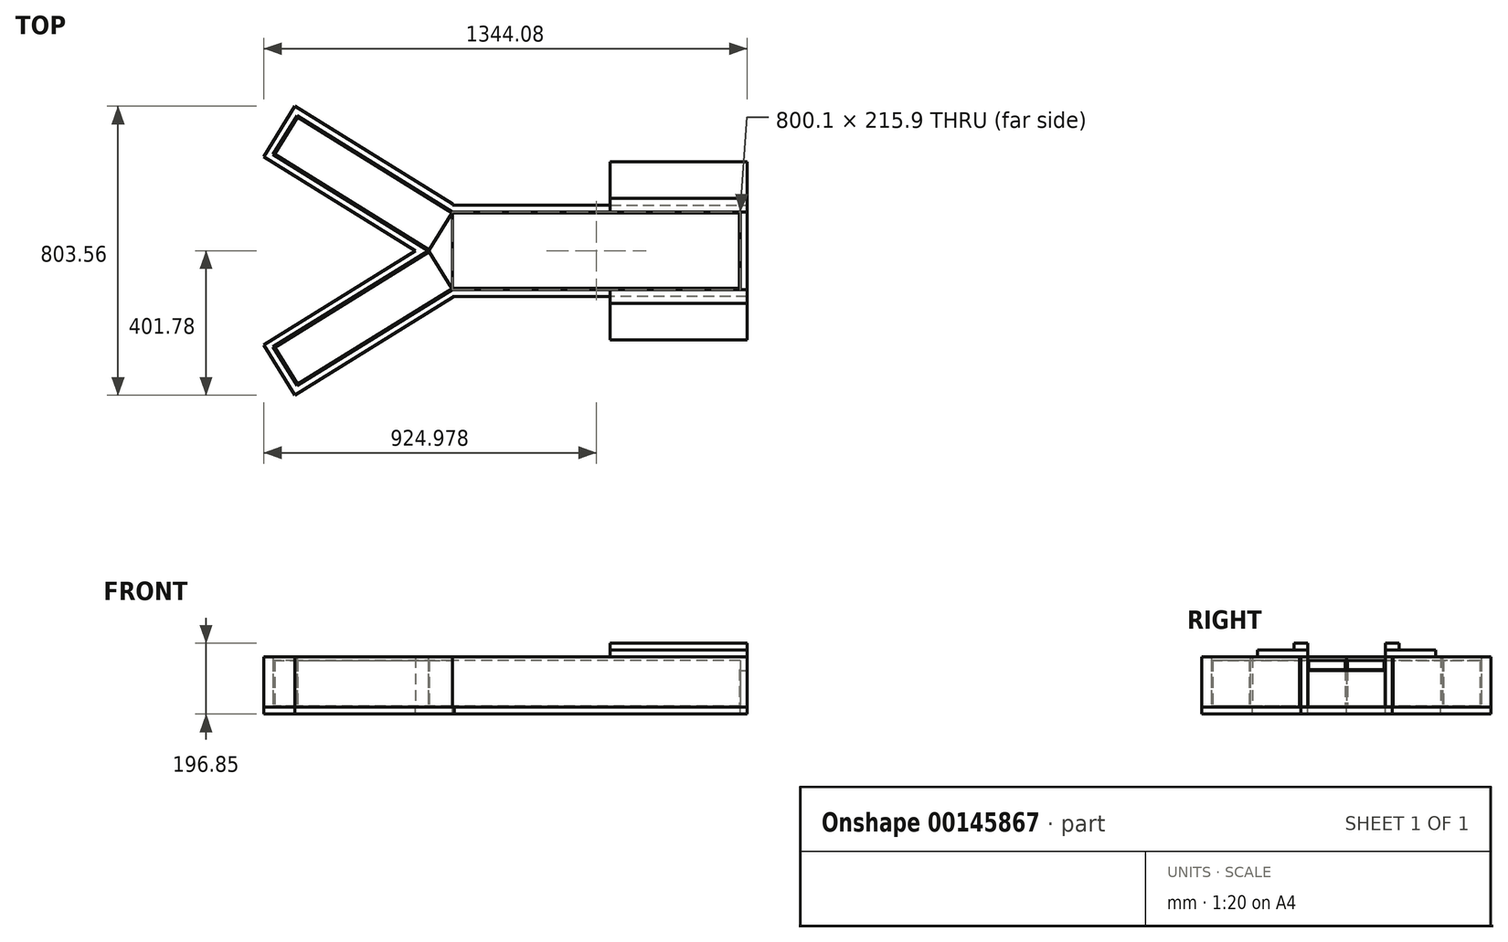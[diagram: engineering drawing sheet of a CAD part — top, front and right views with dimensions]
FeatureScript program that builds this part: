
annotation { "Feature Type Name" : "Feature", "Feature Type Description" : "" }
export const myFeature = defineFeature(function(context is Context, id is Id, definition is map)
    precondition{}
    {
        {
            var Q0;
            Q0=qCreatedBy(makeId("Top.planeOp"),FACE);
            var sketch = newSketch(context, id + "F0", { "sketchPlane" : qUnion([Q0])});
            skLineSegment(sketch, "E0", {"start": v(0, 0) * mm, "end": v(746.46, 0) * mm, "construction": true});
            skLineSegment(sketch, "E1", {"start": v(0, 0) * mm, "end": v(-518.9, 321.58) * mm, "construction": true});
            skLineSegment(sketch, "E2.0.MirrorCS", {"start": v(0, 0) * mm, "end": v(-518.9, -321.58) * mm, "construction": true});
            skLineSegment(sketch, "E3.bottom", {"start": v(746.46, -107.95) * mm, "end": v(-53.64, -107.95) * mm});
            skLineSegment(sketch, "E3.top", {"start": v(746.46, 107.95) * mm, "end": v(-53.64, 107.95) * mm});
            skLineSegment(sketch, "E3.left", {"start": v(746.46, 107.95) * mm, "end": v(746.46, -107.95) * mm});
            skLineSegment(sketch, "E3.right", {"start": v(-53.64, 107.95) * mm, "end": v(-53.64, -107.95) * mm});
            skLineSegment(sketch, "E4", {"start": v(-485.44, 375.56) * mm, "end": v(-552.34, 267.6) * mm});
            skLineSegment(sketch, "E5", {"start": v(-552.34, 267.6) * mm, "end": v(-120.54, 0) * mm});
            skLineSegment(sketch, "E6", {"start": v(-120.54, 0) * mm, "end": v(-53.64, 107.95) * mm});
            skLineSegment(sketch, "E7", {"start": v(-53.64, 107.95) * mm, "end": v(-485.44, 375.56) * mm});
            skLineSegment(sketch, "E8.0.MirrorCS", {"start": v(-53.64, -107.95) * mm, "end": v(-485.44, -375.56) * mm});
            skLineSegment(sketch, "E9.0.MirrorCS", {"start": v(-120.54, 0) * mm, "end": v(-53.64, -107.95) * mm});
            skLineSegment(sketch, "E10.0.MirrorCS", {"start": v(-552.34, -267.6) * mm, "end": v(-120.54, 0) * mm});
            skLineSegment(sketch, "E11.0.MirrorCS", {"start": v(-485.44, -375.56) * mm, "end": v(-552.34, -267.6) * mm});
            skSolve(sketch);
        }
        {
            var Q0;
            Q0=makeQuery(id+"F0.imprint","IMPRINT",FACE,{"disambiguationData":[TD([[makeQuery(id+"F0.imprint","IMPRINT",EDGE,{"derivedFrom":sQuery(id+"F0.wireOp",EDGE,"E4")}),1.0]])]});
            extrude(context, id + "F1", {"entities" : qUnion([Q0]), "depth" : 3.17 * mm});
        }
        {
            var Q0;
            Q0=makeQuery(id+"F0.imprint","IMPRINT",FACE,{"disambiguationData":[TD([[makeQuery(id+"F0.imprint","IMPRINT",EDGE,{"derivedFrom":sQuery(id+"F0.wireOp",EDGE,"E8.0.MirrorCS")}),-1.0]])]});
            extrude(context, id + "F2", {"entities" : qUnion([Q0]), "depth" : 3.17 * mm});
        }
        {
            var Q0;
            Q0=makeQuery(id+"F0.imprint","IMPRINT",FACE,{"disambiguationData":[TD([[makeQuery(id+"F0.imprint","IMPRINT",EDGE,{"derivedFrom":sQuery(id+"F0.wireOp",EDGE,"E3.right")}),-1.0]])]});
            extrude(context, id + "F3", {"entities" : qUnion([Q0]), "depth" : 3.17 * mm});
        }
        {
            var Q0;
            Q0=makeQuery(id+"F0.imprint","IMPRINT",FACE,{"disambiguationData":[TD([[makeQuery(id+"F0.imprint","IMPRINT",EDGE,{"derivedFrom":sQuery(id+"F0.wireOp",EDGE,"E3.bottom")}),-1.0]])]});
            extrude(context, id + "F4", {"entities" : qUnion([Q0]), "depth" : 3.17 * mm});
        }
        {
            var Q0;
            Q0=makeQuery(id+"F4.opExtrude","CAP_FACE",FACE,{"disambiguationData":[OSD([sQuery(id+"F0.wireOp",EDGE,"E3.bottom"),sQuery(id+"F0.wireOp",EDGE,"E3.top"),sQuery(id+"F0.wireOp",EDGE,"E3.left"),sQuery(id+"F0.wireOp",EDGE,"E3.right")])],"isStart":false});
            var sketch = newSketch(context, id + "F5", { "sketchPlane" : qUnion([Q0])});
            skLineSegment(sketch, "E12.0", {"start": v(-53.64, -104.78) * mm, "end": v(743.28, -104.78) * mm});
            skLineSegment(sketch, "E12.2", {"start": v(743.28, 104.78) * mm, "end": v(-53.64, 104.78) * mm});
            skLineSegment(sketch, "E12.3", {"start": v(743.28, -104.78) * mm, "end": v(743.28, 104.78) * mm});
            skLineSegment(sketch, "E13.0", {"start": v(-484.42, -371.18) * mm, "end": v(-55.31, -105.25) * mm});
            skLineSegment(sketch, "E13.1", {"start": v(-547.97, -268.63) * mm, "end": v(-484.42, -371.18) * mm});
            skLineSegment(sketch, "E13.2", {"start": v(-118.87, -2.7) * mm, "end": v(-547.97, -268.63) * mm});
            skLineSegment(sketch, "E14.0", {"start": v(-55.31, 105.25) * mm, "end": v(-484.42, 371.18) * mm});
            skLineSegment(sketch, "E14.2", {"start": v(-547.97, 268.63) * mm, "end": v(-118.87, 2.7) * mm});
            skLineSegment(sketch, "E14.3", {"start": v(-484.42, 371.18) * mm, "end": v(-547.97, 268.63) * mm});
            skLineSegment(sketch, "E15.0.0", {"start": v(-53.64, 107.95) * mm, "end": v(-485.44, 375.56) * mm});
            skLineSegment(sketch, "E15.0.1", {"start": v(-485.44, 375.56) * mm, "end": v(-552.34, 267.6) * mm});
            skLineSegment(sketch, "E15.0.2", {"start": v(-552.34, 267.6) * mm, "end": v(-120.54, 0) * mm});
            skLineSegment(sketch, "E16.0.0", {"start": v(-53.64, -107.95) * mm, "end": v(746.46, -107.95) * mm});
            skLineSegment(sketch, "E16.0.1", {"start": v(746.46, -107.95) * mm, "end": v(746.46, 107.95) * mm});
            skLineSegment(sketch, "E16.0.2", {"start": v(746.46, 107.95) * mm, "end": v(-53.64, 107.95) * mm});
            skLineSegment(sketch, "E17.0.0", {"start": v(-485.44, -375.56) * mm, "end": v(-53.64, -107.95) * mm});
            skLineSegment(sketch, "E17.0.2", {"start": v(-120.54, 0) * mm, "end": v(-552.34, -267.6) * mm});
            skLineSegment(sketch, "E17.0.3", {"start": v(-552.34, -267.6) * mm, "end": v(-485.44, -375.56) * mm});
            skLineSegment(sketch, "E18", {"start": v(-53.64, -104.78) * mm, "end": v(-53.64, -107.95) * mm});
            skLineSegment(sketch, "E19", {"start": v(-55.31, -105.25) * mm, "end": v(-53.64, -107.95) * mm});
            skLineSegment(sketch, "E20", {"start": v(-118.87, 2.7) * mm, "end": v(-120.54, 0) * mm});
            skLineSegment(sketch, "E21", {"start": v(-120.54, 0) * mm, "end": v(-118.87, -2.7) * mm});
            skLineSegment(sketch, "E22", {"start": v(-53.64, 104.78) * mm, "end": v(-53.64, 107.95) * mm});
            skLineSegment(sketch, "E23", {"start": v(-55.31, 105.25) * mm, "end": v(-53.64, 107.95) * mm});
            skLineSegment(sketch, "E24", {"start": v(-484.42, 371.18) * mm, "end": v(-487.11, 372.86) * mm});
            skLineSegment(sketch, "E25", {"start": v(-547.97, 268.63) * mm, "end": v(-550.67, 270.3) * mm});
            skLineSegment(sketch, "E26", {"start": v(-484.42, -371.18) * mm, "end": v(-487.11, -372.86) * mm});
            skLineSegment(sketch, "E27", {"start": v(-547.97, -268.63) * mm, "end": v(-550.67, -270.3) * mm});
            skLineSegment(sketch, "E28", {"start": v(743.28, -104.78) * mm, "end": v(746.46, -104.78) * mm});
            skLineSegment(sketch, "E29", {"start": v(743.28, 104.78) * mm, "end": v(746.46, 104.78) * mm});
            skSolve(sketch);
        }
        {
            var Q0;
            Q0=makeQuery(id+"F5.imprint","IMPRINT",FACE,{"disambiguationData":[TD([[makeQuery(id+"F5.imprint","IMPRINT",EDGE,{"derivedFrom":sQuery(id+"F5.wireOp",EDGE,"E13.0")}),-1.0]])]});
            extrude(context, id + "F6", {"entities" : qUnion([Q0]), "depth" : 127 * mm});
        }
        {
            var Q0;
            Q0=makeQuery(id+"F5.imprint","IMPRINT",FACE,{"disambiguationData":[TD([[makeQuery(id+"F5.imprint","IMPRINT",EDGE,{"derivedFrom":sQuery(id+"F5.wireOp",EDGE,"E13.1")}),-1.0]])]});
            extrude(context, id + "F7", {"entities" : qUnion([Q0]), "depth" : 127 * mm});
        }
        {
            var Q0;
            Q0=makeQuery(id+"F5.imprint","IMPRINT",FACE,{"disambiguationData":[TD([[makeQuery(id+"F5.imprint","IMPRINT",EDGE,{"derivedFrom":sQuery(id+"F5.wireOp",EDGE,"E13.2")}),-1.0]])]});
            extrude(context, id + "F8", {"entities" : qUnion([Q0]), "depth" : 127 * mm});
        }
        {
            var Q0;
            Q0=makeQuery(id+"F5.imprint","IMPRINT",FACE,{"disambiguationData":[TD([[makeQuery(id+"F5.imprint","IMPRINT",EDGE,{"derivedFrom":sQuery(id+"F5.wireOp",EDGE,"E14.2")}),-1.0]])]});
            extrude(context, id + "F9", {"entities" : qUnion([Q0]), "depth" : 127 * mm});
        }
        {
            var Q0;
            Q0=makeQuery(id+"F5.imprint","IMPRINT",FACE,{"disambiguationData":[TD([[makeQuery(id+"F5.imprint","IMPRINT",EDGE,{"derivedFrom":sQuery(id+"F5.wireOp",EDGE,"E14.0")}),-1.0]])]});
            extrude(context, id + "F10", {"entities" : qUnion([Q0]), "depth" : 127 * mm});
        }
        {
            var Q0;
            Q0=makeQuery(id+"F5.imprint","IMPRINT",FACE,{"disambiguationData":[TD([[makeQuery(id+"F5.imprint","IMPRINT",EDGE,{"derivedFrom":sQuery(id+"F5.wireOp",EDGE,"E14.3")}),-1.0]])]});
            extrude(context, id + "F11", {"entities" : qUnion([Q0]), "depth" : 127 * mm});
        }
        {
            var Q0;
            Q0=makeQuery(id+"F5.imprint","IMPRINT",FACE,{"disambiguationData":[TD([[makeQuery(id+"F5.imprint","IMPRINT",EDGE,{"derivedFrom":sQuery(id+"F5.wireOp",EDGE,"E12.0")}),-1.0]])]});
            extrude(context, id + "F12", {"entities" : qUnion([Q0]), "depth" : 127 * mm});
        }
        {
            var Q0;
            Q0=makeQuery(id+"F5.imprint","IMPRINT",FACE,{"disambiguationData":[TD([[makeQuery(id+"F5.imprint","IMPRINT",EDGE,{"derivedFrom":sQuery(id+"F5.wireOp",EDGE,"E12.3")}),-1.0]])]});
            extrude(context, id + "F13", {"entities" : qUnion([Q0]), "depth" : 101.6 * mm});
        }
        {
            var Q0;
            Q0=makeQuery(id+"F5.imprint","IMPRINT",FACE,{"disambiguationData":[TD([[makeQuery(id+"F5.imprint","IMPRINT",EDGE,{"derivedFrom":sQuery(id+"F5.wireOp",EDGE,"E12.2")}),-1.0]])]});
            extrude(context, id + "F14", {"entities" : qUnion([Q0]), "depth" : 127 * mm});
        }
        {
            var Q0;
            Q0=makeQuery(id+"F4.opExtrude","CAP_FACE",FACE,{"disambiguationData":[OSD([sQuery(id+"F0.wireOp",EDGE,"E3.bottom"),sQuery(id+"F0.wireOp",EDGE,"E3.top"),sQuery(id+"F0.wireOp",EDGE,"E3.left"),sQuery(id+"F0.wireOp",EDGE,"E3.right")])],"isStart":true});
            var sketch = newSketch(context, id + "F15", { "sketchPlane" : qUnion([Q0])});
            skLineSegment(sketch, "E30.0", {"start": v(765.5, 127) * mm, "end": v(-48.22, 127) * mm});
            skLineSegment(sketch, "E30.1", {"start": v(765.5, -127) * mm, "end": v(765.5, 127) * mm});
            skLineSegment(sketch, "E30.2", {"start": v(-48.22, -127) * mm, "end": v(765.5, -127) * mm});
            skLineSegment(sketch, "E31.0", {"start": v(-48.22, 127) * mm, "end": v(-491.6, 401.78) * mm});
            skLineSegment(sketch, "E31.2", {"start": v(-578.57, 261.45) * mm, "end": v(-156.7, 0) * mm});
            skLineSegment(sketch, "E31.3", {"start": v(-491.6, 401.78) * mm, "end": v(-578.57, 261.45) * mm});
            skLineSegment(sketch, "E32.0", {"start": v(-491.6, -401.78) * mm, "end": v(-48.22, -127) * mm});
            skLineSegment(sketch, "E32.1", {"start": v(-578.57, -261.45) * mm, "end": v(-491.6, -401.78) * mm});
            skLineSegment(sketch, "E32.2", {"start": v(-156.7, 0) * mm, "end": v(-578.57, -261.45) * mm});
            skPoint(sketch, "E33.start.orphan", {"position": v(-122.08, 0) * mm});
            skSolve(sketch);
        }
        {
            var Q0;
            Q0=makeQuery(id+"F15.imprint","IMPRINT",FACE,{"disambiguationData":[TD([[makeQuery(id+"F15.imprint","IMPRINT",EDGE,{"derivedFrom":sQuery(id+"F15.wireOp",EDGE,"E30.0")}),1.0]])]});
            extrude(context, id + "F16", {"entities" : qUnion([Q0]), "depth" : 19.05 * mm});
        }
        {
            var Q0;
            Q0=makeQuery(id+"F16.opExtrude","CAP_FACE",FACE,{"disambiguationData":[OSD([sQuery(id+"F0.wireOp",EDGE,"E3.bottom"),sQuery(id+"F0.wireOp",EDGE,"E3.top"),sQuery(id+"F0.wireOp",EDGE,"E3.left"),sQuery(id+"F0.wireOp",EDGE,"E3.right"),sQuery(id+"F15.wireOp",EDGE,"E30.0"),sQuery(id+"F15.wireOp",EDGE,"E30.1"),sQuery(id+"F15.wireOp",EDGE,"E30.2"),sQuery(id+"F15.wireOp",EDGE,"E31.0"),sQuery(id+"F15.wireOp",EDGE,"E31.2"),sQuery(id+"F15.wireOp",EDGE,"E31.3"),sQuery(id+"F15.wireOp",EDGE,"E32.0"),sQuery(id+"F15.wireOp",EDGE,"E32.1"),sQuery(id+"F15.wireOp",EDGE,"E32.2")])],"isStart":true});
            var sketch = newSketch(context, id + "F17", { "sketchPlane" : qUnion([Q0])});
            skLineSegment(sketch, "E34.0", {"start": v(-53.64, -107.95) * mm, "end": v(746.46, -107.95) * mm});
            skLineSegment(sketch, "E34.1", {"start": v(-485.44, -375.56) * mm, "end": v(-53.64, -107.95) * mm});
            skLineSegment(sketch, "E34.2", {"start": v(-552.34, -267.6) * mm, "end": v(-485.44, -375.56) * mm});
            skLineSegment(sketch, "E34.3", {"start": v(-120.54, 0) * mm, "end": v(-552.34, -267.6) * mm});
            skLineSegment(sketch, "E34.4", {"start": v(-552.34, 267.6) * mm, "end": v(-120.54, 0) * mm});
            skLineSegment(sketch, "E34.5", {"start": v(746.46, -107.95) * mm, "end": v(746.46, 107.95) * mm});
            skLineSegment(sketch, "E34.6", {"start": v(-485.44, 375.56) * mm, "end": v(-552.34, 267.6) * mm});
            skLineSegment(sketch, "E34.7", {"start": v(-53.64, 107.95) * mm, "end": v(-485.44, 375.56) * mm});
            skLineSegment(sketch, "E34.8", {"start": v(746.46, 107.95) * mm, "end": v(-53.64, 107.95) * mm});
            skLineSegment(sketch, "E35.0.0", {"start": v(765.5, -127) * mm, "end": v(765.5, 127) * mm});
            skLineSegment(sketch, "E35.0.1", {"start": v(765.5, 127) * mm, "end": v(-48.22, 127) * mm});
            skLineSegment(sketch, "E35.0.2", {"start": v(-48.22, 127) * mm, "end": v(-491.6, 401.78) * mm});
            skLineSegment(sketch, "E35.0.3", {"start": v(-491.6, 401.78) * mm, "end": v(-578.57, 261.45) * mm});
            skLineSegment(sketch, "E35.0.4", {"start": v(-578.57, 261.45) * mm, "end": v(-156.7, 0) * mm});
            skLineSegment(sketch, "E35.0.5", {"start": v(-156.7, 0) * mm, "end": v(-578.57, -261.45) * mm});
            skLineSegment(sketch, "E35.0.6", {"start": v(-578.57, -261.45) * mm, "end": v(-491.6, -401.78) * mm});
            skLineSegment(sketch, "E35.0.7", {"start": v(-491.6, -401.78) * mm, "end": v(-48.22, -127) * mm});
            skLineSegment(sketch, "E35.0.8", {"start": v(-48.22, -127) * mm, "end": v(765.5, -127) * mm});
            skLineSegment(sketch, "E36", {"start": v(-552.34, -267.6) * mm, "end": v(-568.54, -277.64) * mm});
            skLineSegment(sketch, "E37", {"start": v(-485.44, -375.56) * mm, "end": v(-501.63, -385.6) * mm});
            skLineSegment(sketch, "E38", {"start": v(-552.34, 267.6) * mm, "end": v(-568.54, 277.64) * mm});
            skLineSegment(sketch, "E39", {"start": v(-485.44, 375.56) * mm, "end": v(-501.63, 385.6) * mm});
            skLineSegment(sketch, "E40", {"start": v(-156.7, 0) * mm, "end": v(-120.54, 0) * mm});
            skLineSegment(sketch, "E41", {"start": v(-53.64, 107.95) * mm, "end": v(-53.64, 130.36) * mm});
            skLineSegment(sketch, "E42", {"start": v(-48.22, 127) * mm, "end": v(-53.64, 127) * mm});
            skLineSegment(sketch, "E43", {"start": v(-53.64, -107.95) * mm, "end": v(-53.64, -130.36) * mm});
            skLineSegment(sketch, "E44", {"start": v(-48.22, -127) * mm, "end": v(-53.64, -127) * mm});
            skLineSegment(sketch, "E45", {"start": v(746.46, 107.95) * mm, "end": v(765.5, 107.95) * mm});
            skLineSegment(sketch, "E46", {"start": v(746.46, -107.95) * mm, "end": v(765.5, -107.95) * mm});
            skSolve(sketch);
        }
        {
            var Q0;
            {var subQ3=sQuery(id+"F17.wireOp",EDGE,"E34.0");Q0=makeQuery(id+"F17.imprint","IMPRINT",FACE,{"disambiguationData":[TD([[makeQuery(id+"F17.imprint","IMPRINT",EDGE,{"derivedFrom":subQ3}),1.0]])]});}
            var Q1;
            {var subQ4=sQuery(id+"F17.wireOp",EDGE,"E34.1");Q1=makeQuery(id+"F17.imprint","IMPRINT",FACE,{"disambiguationData":[TD([[makeQuery(id+"F17.imprint","IMPRINT",EDGE,{"derivedFrom":subQ4}),-1.0]])]});}
            var Q2;
            Q2=makeQuery(id+"F17.imprint","IMPRINT",FACE,{"disambiguationData":[TD([[makeQuery(id+"F17.imprint","IMPRINT",EDGE,{"derivedFrom":sQuery(id+"F17.wireOp",EDGE,"E34.3")}),-1.0]])]});
            var Q3;
            Q3=makeQuery(id+"F17.imprint","IMPRINT",FACE,{"disambiguationData":[TD([[makeQuery(id+"F17.imprint","IMPRINT",EDGE,{"derivedFrom":sQuery(id+"F17.wireOp",EDGE,"E34.4")}),-1.0]])]});
            var Q4;
            {var subQ4=sQuery(id+"F17.wireOp",EDGE,"E34.7");Q4=makeQuery(id+"F17.imprint","IMPRINT",FACE,{"disambiguationData":[TD([[makeQuery(id+"F17.imprint","IMPRINT",EDGE,{"derivedFrom":subQ4}),-1.0]])]});}
            var Q5;
            {var subQ2=sQuery(id+"F17.wireOp",EDGE,"E34.8");Q5=makeQuery(id+"F17.imprint","IMPRINT",FACE,{"disambiguationData":[TD([[makeQuery(id+"F17.imprint","IMPRINT",EDGE,{"derivedFrom":subQ2}),-1.0]])]});}
            var Q6;
            Q6=makeQuery(id+"F17.imprint","IMPRINT",FACE,{"disambiguationData":[TD([[makeQuery(id+"F17.imprint","IMPRINT",EDGE,{"derivedFrom":sQuery(id+"F17.wireOp",EDGE,"E34.6")}),-1.0]])]});
            var Q7;
            Q7=makeQuery(id+"F17.imprint","IMPRINT",FACE,{"disambiguationData":[TD([[makeQuery(id+"F17.imprint","IMPRINT",EDGE,{"derivedFrom":sQuery(id+"F17.wireOp",EDGE,"E34.2")}),-1.0]])]});
            extrude(context, id + "F18", {"entities" : qUnion([Q0, Q1, Q2, Q3, Q4, Q5, Q6, Q7]), "depth" : 139.7 * mm});
        }
        {
            var Q0;
            Q0=makeQuery(id+"F17.imprint","IMPRINT",FACE,{"disambiguationData":[TD([[makeQuery(id+"F17.imprint","IMPRINT",EDGE,{"derivedFrom":sQuery(id+"F17.wireOp",EDGE,"E34.5")}),1.0]])]});
            extrude(context, id + "F19", {"entities" : qUnion([Q0]), "depth" : 101.6 * mm});
        }
        {
            var Q0;
            Q0=makeQuery(id+"F18.opExtrude","CAP_FACE",FACE,{"disambiguationData":[OSD([sQuery(id+"F17.wireOp",EDGE,"E34.0"),sQuery(id+"F17.wireOp",EDGE,"E34.1"),sQuery(id+"F17.wireOp",EDGE,"E34.2"),sQuery(id+"F17.wireOp",EDGE,"E34.3"),sQuery(id+"F17.wireOp",EDGE,"E34.4"),sQuery(id+"F17.wireOp",EDGE,"E34.6"),sQuery(id+"F17.wireOp",EDGE,"E34.7"),sQuery(id+"F17.wireOp",EDGE,"E34.8"),sQuery(id+"F17.wireOp",EDGE,"E35.0.0"),sQuery(id+"F17.wireOp",EDGE,"E35.0.1"),sQuery(id+"F17.wireOp",EDGE,"E35.0.2"),sQuery(id+"F17.wireOp",EDGE,"E35.0.3"),sQuery(id+"F17.wireOp",EDGE,"E35.0.4"),sQuery(id+"F17.wireOp",EDGE,"E35.0.5"),sQuery(id+"F17.wireOp",EDGE,"E35.0.6"),sQuery(id+"F17.wireOp",EDGE,"E35.0.7"),sQuery(id+"F17.wireOp",EDGE,"E35.0.8"),sQuery(id+"F17.wireOp",EDGE,"E41"),sQuery(id+"F17.wireOp",EDGE,"E42"),sQuery(id+"F17.wireOp",EDGE,"E43"),sQuery(id+"F17.wireOp",EDGE,"E44"),sQuery(id+"F17.wireOp",EDGE,"E45"),sQuery(id+"F17.wireOp",EDGE,"E46")])],"isStart":false});
            var sketch = newSketch(context, id + "F20", { "sketchPlane" : qUnion([Q0])});
            skLineSegment(sketch, "E47.bottom", {"start": v(765.5, 107.95) * mm, "end": v(384.5, 107.95) * mm});
            skLineSegment(sketch, "E47.top", {"start": v(765.5, 247.65) * mm, "end": v(384.5, 247.65) * mm});
            skLineSegment(sketch, "E47.left", {"start": v(765.5, 107.95) * mm, "end": v(765.5, 247.65) * mm});
            skLineSegment(sketch, "E47.right", {"start": v(384.5, 107.95) * mm, "end": v(384.5, 247.65) * mm});
            skLineSegment(sketch, "E48.bottom", {"start": v(765.5, -107.95) * mm, "end": v(384.5, -107.95) * mm});
            skLineSegment(sketch, "E48.top", {"start": v(765.5, -247.65) * mm, "end": v(384.5, -247.65) * mm});
            skLineSegment(sketch, "E48.left", {"start": v(765.5, -107.95) * mm, "end": v(765.5, -247.65) * mm});
            skLineSegment(sketch, "E48.right", {"start": v(384.5, -107.95) * mm, "end": v(384.5, -247.65) * mm});
            skSolve(sketch);
        }
        {
            var Q0;
            {var subQ3=sQuery(id+"F20.wireOp",EDGE,"E48.top");Q0=makeQuery(id+"F20.imprint","IMPRINT",FACE,{"disambiguationData":[TD([[makeQuery(id+"F20.imprint","IMPRINT",EDGE,{"derivedFrom":subQ3}),-1.0]])]});}
            var Q1;
            {var subQ5=sQuery(id+"F20.wireOp",EDGE,"E47.top");Q1=makeQuery(id+"F20.imprint","IMPRINT",FACE,{"disambiguationData":[TD([[makeQuery(id+"F20.imprint","IMPRINT",EDGE,{"derivedFrom":subQ5}),1.0]])]});}
            var Q2;
            {var subQ5=sQuery(id+"F20.wireOp",EDGE,"E48.bottom");Q2=makeQuery(id+"F20.imprint","IMPRINT",FACE,{"disambiguationData":[TD([[makeQuery(id+"F20.imprint","IMPRINT",EDGE,{"derivedFrom":subQ5}),1.0]])]});}
            var Q3;
            {var subQ5=sQuery(id+"F20.wireOp",EDGE,"E47.bottom");Q3=makeQuery(id+"F20.imprint","IMPRINT",FACE,{"disambiguationData":[TD([[makeQuery(id+"F20.imprint","IMPRINT",EDGE,{"derivedFrom":subQ5}),-1.0]])]});}
            extrude(context, id + "F21", {"entities" : qUnion([Q0, Q1, Q2, Q3]), "depth" : 19.05 * mm});
        }
        {
            var Q0;
            Q0=makeQuery(id+"F21.opExtrude","CAP_FACE",FACE,{"disambiguationData":[OSD([sQuery(id+"F20.wireOp",EDGE,"E48.bottom"),sQuery(id+"F20.wireOp",EDGE,"E48.top"),sQuery(id+"F20.wireOp",EDGE,"E48.left"),sQuery(id+"F20.wireOp",EDGE,"E48.right")])],"isStart":false});
            var sketch = newSketch(context, id + "F22", { "sketchPlane" : qUnion([Q0])});
            skLineSegment(sketch, "E49.bottom", {"start": v(384.5, -107.95) * mm, "end": v(765.5, -107.95) * mm});
            skLineSegment(sketch, "E49.top", {"start": v(384.5, -146.05) * mm, "end": v(765.5, -146.05) * mm});
            skLineSegment(sketch, "E49.left", {"start": v(384.5, -107.95) * mm, "end": v(384.5, -146.05) * mm});
            skLineSegment(sketch, "E49.right", {"start": v(765.5, -107.95) * mm, "end": v(765.5, -146.05) * mm});
            skLineSegment(sketch, "E50.bottom", {"start": v(384.5, 107.95) * mm, "end": v(765.5, 107.95) * mm});
            skLineSegment(sketch, "E50.top", {"start": v(384.5, 146.05) * mm, "end": v(765.5, 146.05) * mm});
            skLineSegment(sketch, "E50.left", {"start": v(384.5, 107.95) * mm, "end": v(384.5, 146.05) * mm});
            skLineSegment(sketch, "E50.right", {"start": v(765.5, 107.95) * mm, "end": v(765.5, 146.05) * mm});
            skSolve(sketch);
        }
        {
            var Q0;
            Q0=qSketchRegion(id+"F22",true);
            extrude(context, id + "F23", {"entities" : qUnion([Q0]), "depth" : 19.05 * mm});
        }
    });
